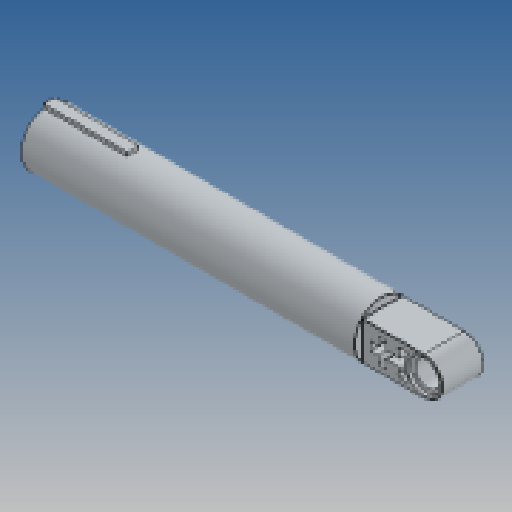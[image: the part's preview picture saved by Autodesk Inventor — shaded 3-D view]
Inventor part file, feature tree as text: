
AUTODESK INVENTOR PART (.ipt)
format: ipt  version: 2025 (Build 290162010, 162A)  size: 301,568 bytes
history: native  units: mm
features: sketch x7, extrude x6, fillet x2, projected_geometry x2, revolve x1
ambient origin geometry x8: Origin, YZ Plane, XZ Plane, XY Plane, X Axis, Y Axis, Z Axis, Center Point
bodies: Volumenkörper1 (feature_tree)
feature tree (18):
  revolve  "Umdrehung1"
  extrude  "Extrusion1"  Depth=10.9mm
  extrude  "Extrusion2"  Depth=8.8mm
  extrude  "Extrusion3"  Depth=2.2mm
  extrude  "Extrusion4"  Depth=16.4mm TaperAngle=0.0deg
  extrude  "Extrusion5"  Depth=12.0mm
  extrude  "Extrusion6"  Depth=0.4mm
  fillet  "Rundung1"  Radius=1.1mm
  fillet  "Rundung2"  Radius=8.0mm
  sketch  "Skizze1"  dims[d0=65.0mm d1=10.9mm]
  sketch  "Skizze2"  dims[d2=63.0mm d3=8.8mm]
  sketch  "Skizze3"  dims[d4=90.0deg d5=2.2mm]
  sketch  "Skizze4"  dims[d6=12.2mm d7=16.4mm d8=0.0mm]
  sketch  "Skizze5"  dims[d9=7.4mm d10=12.0mm]
  sketch  "Skizze6"  dims[d11=4.8mm d12=0.4mm d13=1.1mm d14=8.0mm]
  sketch  "Skizze7"  dims[d15=1.6mm d16=8.0mm d17=0.0mm d18=6.4mm d19=0.8mm d20=0.0mm d21=0.8mm d22=0.0mm d23=2.4mm d24=0.3mm d25=0.0mm d26=0.8mm d27=0.0mm d28=0.1mm d29=0.1mm]
  projected_geometry  "Projizierte Kontur1"
  projected_geometry  "Projizierte Kontur2"
